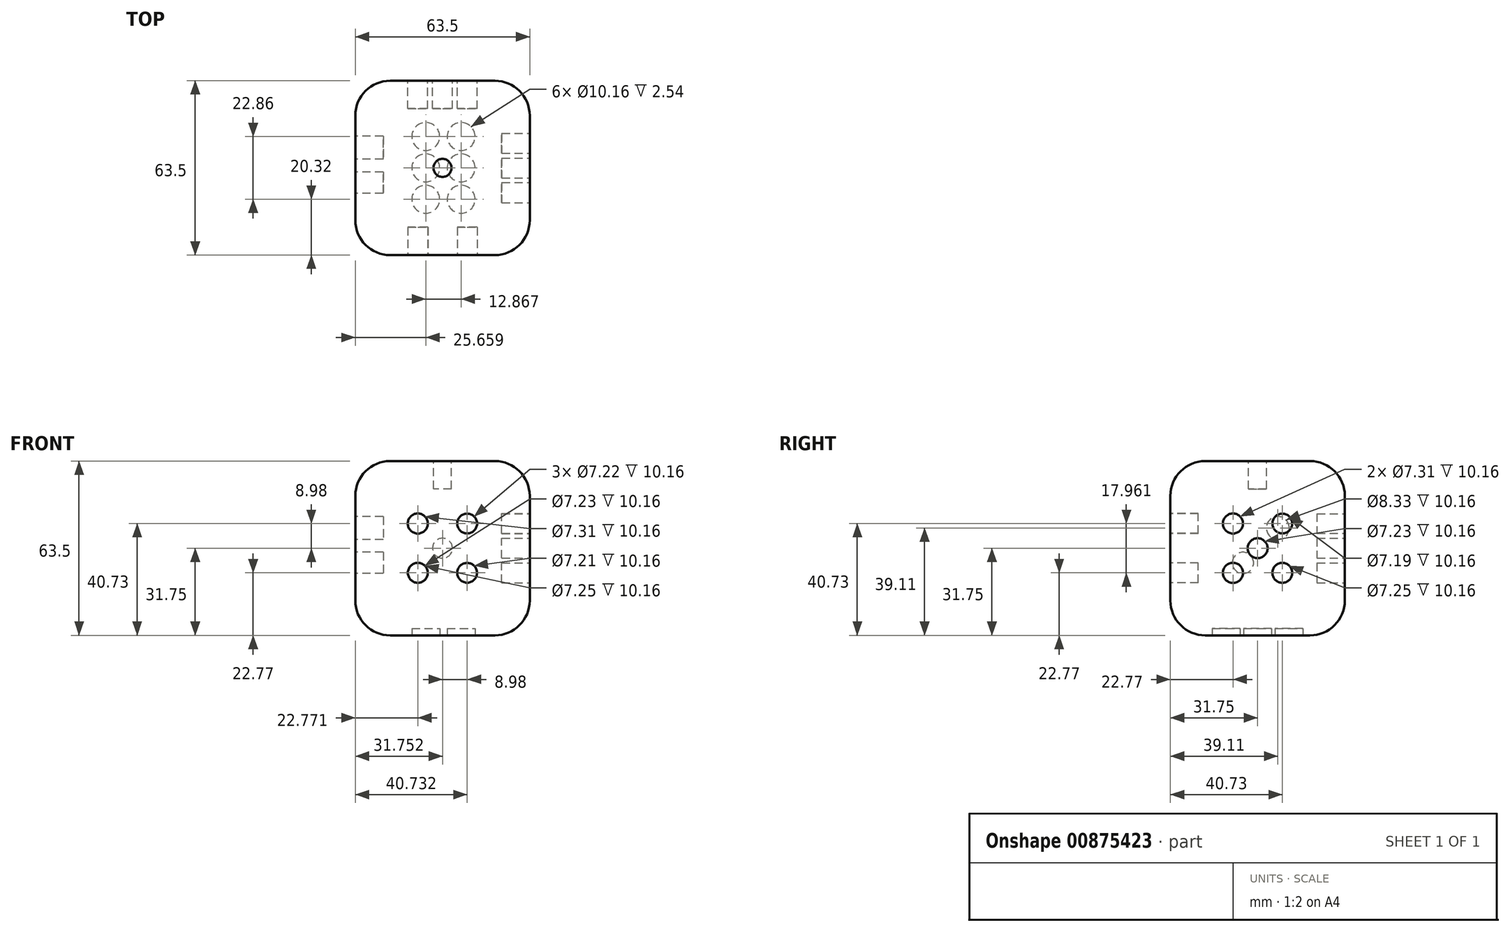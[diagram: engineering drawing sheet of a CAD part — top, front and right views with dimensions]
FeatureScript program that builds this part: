
annotation { "Feature Type Name" : "Feature", "Feature Type Description" : "" }
export const myFeature = defineFeature(function(context is Context, id is Id, definition is map)
    precondition{}
    {
        {
            var Q0;
            Q0=qCreatedBy(makeId("Top.planeOp"),FACE);
            var sketch = newSketch(context, id + "F0", { "sketchPlane" : qUnion([Q0])});
            skLineSegment(sketch, "E0.bottom", {"start": v(-137.5, 64.58) * mm, "end": v(-74, 64.58) * mm});
            skLineSegment(sketch, "E0.top", {"start": v(-137.5, 1.08) * mm, "end": v(-74, 1.08) * mm});
            skLineSegment(sketch, "E0.left", {"start": v(-137.5, 64.58) * mm, "end": v(-137.5, 1.08) * mm});
            skLineSegment(sketch, "E0.right", {"start": v(-74, 64.58) * mm, "end": v(-74, 1.08) * mm});
            skSolve(sketch);
        }
        {
            var Q0;
            Q0=makeQuery(id+"F0.imprint","IMPRINT",FACE,{"disambiguationData":[TD([[makeQuery(id+"F0.imprint","IMPRINT",EDGE,{"derivedFrom":sQuery(id+"F0.wireOp",EDGE,"E0.bottom")}),-1.0]])]});
            extrude(context, id + "F1", {"entities" : qUnion([Q0]), "depth" : 63.5 * mm, "offsetDistance" : 25.4 * mm});
        }
        {
            var Q0;
            Q0=makeQuery(id+"F1.opExtrude","CAP_EDGE",EDGE,{"disambiguationData":[OSD([sQuery(id+"F0.wireOp",EDGE,"E0.right")])],"isStart":true});
            var Q1;
            Q1=makeQuery(id+"F1.opExtrude","CAP_EDGE",EDGE,{"disambiguationData":[OSD([sQuery(id+"F0.wireOp",EDGE,"E0.left")])],"isStart":true});
            var Q2;
            Q2=makeQuery(id+"F1.opExtrude","CAP_EDGE",EDGE,{"disambiguationData":[OSD([sQuery(id+"F0.wireOp",EDGE,"E0.top")])],"isStart":true});
            var Q3;
            Q3=makeQuery(id+"F1.opExtrude","SWEPT_EDGE",EDGE,{"disambiguationData":[OSD([sQuery(id+"F0.wireOp",EDGE,"E0.top"),sQuery(id+"F0.wireOp",EDGE,"E0.left")])]});
            var Q4;
            Q4=makeQuery(id+"F1.opExtrude","SWEPT_EDGE",EDGE,{"disambiguationData":[OSD([sQuery(id+"F0.wireOp",EDGE,"E0.top"),sQuery(id+"F0.wireOp",EDGE,"E0.right")])]});
            var Q5;
            Q5=makeQuery(id+"F1.opExtrude","CAP_EDGE",EDGE,{"disambiguationData":[OSD([sQuery(id+"F0.wireOp",EDGE,"E0.left")])],"isStart":false});
            var Q6;
            Q6=makeQuery(id+"F1.opExtrude","CAP_EDGE",EDGE,{"disambiguationData":[OSD([sQuery(id+"F0.wireOp",EDGE,"E0.bottom")])],"isStart":true});
            var Q7;
            Q7=makeQuery(id+"F1.opExtrude","SWEPT_EDGE",EDGE,{"disambiguationData":[OSD([sQuery(id+"F0.wireOp",EDGE,"E0.bottom"),sQuery(id+"F0.wireOp",EDGE,"E0.left")])]});
            var Q8;
            Q8=makeQuery(id+"F1.opExtrude","CAP_EDGE",EDGE,{"disambiguationData":[OSD([sQuery(id+"F0.wireOp",EDGE,"E0.bottom")])],"isStart":false});
            var Q9;
            Q9=makeQuery(id+"F1.opExtrude","SWEPT_EDGE",EDGE,{"disambiguationData":[OSD([sQuery(id+"F0.wireOp",EDGE,"E0.bottom"),sQuery(id+"F0.wireOp",EDGE,"E0.right")])]});
            var Q10;
            Q10=makeQuery(id+"F1.opExtrude","CAP_EDGE",EDGE,{"disambiguationData":[OSD([sQuery(id+"F0.wireOp",EDGE,"E0.right")])],"isStart":false});
            var Q11;
            Q11=makeQuery(id+"F1.opExtrude","CAP_EDGE",EDGE,{"disambiguationData":[OSD([sQuery(id+"F0.wireOp",EDGE,"E0.top")])],"isStart":false});
            fillet(context, id + "F2", {"entities" : qUnion([Q0, Q1, Q2, Q3, Q4, Q5, Q6, Q7, Q8, Q9, Q10, Q11]), "radius" : 12.7 * mm, "tangentPropagation" : true, "allowEdgeOverflow" : false});
        }
        {
            var Q0;
            Q0=makeQuery(id+"F1.opExtrude","CAP_FACE",FACE,{"disambiguationData":[OSD([sQuery(id+"F0.wireOp",EDGE,"E0.bottom"),sQuery(id+"F0.wireOp",EDGE,"E0.top"),sQuery(id+"F0.wireOp",EDGE,"E0.left"),sQuery(id+"F0.wireOp",EDGE,"E0.right")])],"isStart":false});
            var sketch = newSketch(context, id + "F3", { "sketchPlane" : qUnion([Q0])});
            skLineSegment(sketch, "E1.0.0", {"start": v(-124.8, 13.78) * mm, "end": v(-86.7, 13.78) * mm});
            skLineSegment(sketch, "E1.0.1", {"start": v(-86.7, 13.78) * mm, "end": v(-86.7, 51.88) * mm});
            skLineSegment(sketch, "E1.0.2", {"start": v(-86.7, 51.88) * mm, "end": v(-124.8, 51.88) * mm});
            skLineSegment(sketch, "E1.0.3", {"start": v(-124.8, 51.88) * mm, "end": v(-124.8, 13.78) * mm});
            skLineSegment(sketch, "E2", {"start": v(-105.76, 51.88) * mm, "end": v(-105.76, 13.78) * mm, "construction": true});
            skLineSegment(sketch, "E3", {"start": v(-124.8, 32.83) * mm, "end": v(-86.7, 32.83) * mm, "construction": true});
            skCircle(sketch, "E4", {"center": v(-105.76, 32.83) * mm, "radius": 3.29 * mm});
            skSolve(sketch);
        }
        {
            var Q0;
            Q0=makeQuery(id+"F3.imprint","IMPRINT",FACE,{"disambiguationData":[TD([[makeQuery(id+"F3.imprint","IMPRINT",EDGE,{"derivedFrom":sQuery(id+"F3.wireOp",EDGE,"E4")}),1.0]])]});
            var Q1;
            Q1=sQuery(id+"F3.wireOp",EDGE,"E4");
            extrude(context, id + "F4", {"entities" : qUnion([Q0]), "operationType" : NewBodyOperationType.REMOVE, "surfaceEntities" : qUnion([Q1]), "oppositeDirection" : true, "depth" : 10.16 * mm, "offsetDistance" : 25.4 * mm});
        }
        {
            var Q0;
            Q0=makeQuery(id+"F1.opExtrude","CAP_FACE",FACE,{"disambiguationData":[OSD([sQuery(id+"F0.wireOp",EDGE,"E0.bottom"),sQuery(id+"F0.wireOp",EDGE,"E0.top"),sQuery(id+"F0.wireOp",EDGE,"E0.left"),sQuery(id+"F0.wireOp",EDGE,"E0.right")])],"isStart":true});
            var sketch = newSketch(context, id + "F5", { "sketchPlane" : qUnion([Q0])});
            skLineSegment(sketch, "E5.0.0", {"start": v(-124.8, -51.88) * mm, "end": v(-86.7, -51.88) * mm});
            skLineSegment(sketch, "E5.0.1", {"start": v(-86.7, -51.88) * mm, "end": v(-86.7, -13.78) * mm});
            skLineSegment(sketch, "E5.0.2", {"start": v(-86.7, -13.78) * mm, "end": v(-124.8, -13.78) * mm});
            skLineSegment(sketch, "E5.0.3", {"start": v(-124.8, -13.78) * mm, "end": v(-124.8, -51.88) * mm});
            skCircle(sketch, "E6", {"center": v(-111.85, -32.83) * mm, "radius": 5.08 * mm});
            skCircle(sketch, "E7", {"center": v(-111.85, -44.26) * mm, "radius": 5.08 * mm});
            skCircle(sketch, "E8", {"center": v(-98.98, -21.4) * mm, "radius": 5.08 * mm});
            skCircle(sketch, "E9", {"center": v(-98.98, -32.83) * mm, "radius": 5.08 * mm});
            skCircle(sketch, "E10", {"center": v(-98.98, -44.26) * mm, "radius": 5.08 * mm});
            skCircle(sketch, "E11", {"center": v(-111.85, -21.4) * mm, "radius": 5.08 * mm});
            skSolve(sketch);
        }
        {
            var Q0;
            Q0=makeQuery(id+"F5.imprint","IMPRINT",FACE,{"disambiguationData":[TD([[makeQuery(id+"F5.imprint","IMPRINT",EDGE,{"derivedFrom":sQuery(id+"F5.wireOp",EDGE,"E11")}),1.0]])]});
            var Q1;
            Q1=makeQuery(id+"F5.imprint","IMPRINT",FACE,{"disambiguationData":[TD([[makeQuery(id+"F5.imprint","IMPRINT",EDGE,{"derivedFrom":sQuery(id+"F5.wireOp",EDGE,"E8")}),1.0]])]});
            var Q2;
            Q2=makeQuery(id+"F5.imprint","IMPRINT",FACE,{"disambiguationData":[TD([[makeQuery(id+"F5.imprint","IMPRINT",EDGE,{"derivedFrom":sQuery(id+"F5.wireOp",EDGE,"E6")}),1.0]])]});
            var Q3;
            Q3=makeQuery(id+"F5.imprint","IMPRINT",FACE,{"disambiguationData":[TD([[makeQuery(id+"F5.imprint","IMPRINT",EDGE,{"derivedFrom":sQuery(id+"F5.wireOp",EDGE,"E9")}),1.0]])]});
            var Q4;
            Q4=makeQuery(id+"F5.imprint","IMPRINT",FACE,{"disambiguationData":[TD([[makeQuery(id+"F5.imprint","IMPRINT",EDGE,{"derivedFrom":sQuery(id+"F5.wireOp",EDGE,"E7")}),1.0]])]});
            var Q5;
            Q5=makeQuery(id+"F5.imprint","IMPRINT",FACE,{"disambiguationData":[TD([[makeQuery(id+"F5.imprint","IMPRINT",EDGE,{"derivedFrom":sQuery(id+"F5.wireOp",EDGE,"E10")}),1.0]])]});
            extrude(context, id + "F6", {"entities" : qUnion([Q0, Q1, Q2, Q3, Q4, Q5]), "operationType" : NewBodyOperationType.REMOVE, "oppositeDirection" : true, "depth" : 2.54 * mm, "offsetDistance" : 25.4 * mm});
        }
        {
            var Q0;
            Q0=makeQuery(id+"F1.opExtrude","SWEPT_FACE",FACE,{"disambiguationData":[OSD([sQuery(id+"F0.wireOp",EDGE,"E0.left")])]});
            var sketch = newSketch(context, id + "F7", { "sketchPlane" : qUnion([Q0])});
            skLineSegment(sketch, "E12.0.0", {"start": v(-51.88, 50.8) * mm, "end": v(-51.88, 12.7) * mm});
            skLineSegment(sketch, "E12.0.1", {"start": v(-51.88, 12.7) * mm, "end": v(-13.78, 12.7) * mm});
            skLineSegment(sketch, "E12.0.2", {"start": v(-13.78, 12.7) * mm, "end": v(-13.78, 50.8) * mm});
            skLineSegment(sketch, "E12.0.3", {"start": v(-13.78, 50.8) * mm, "end": v(-51.88, 50.8) * mm});
            skCircle(sketch, "E13", {"center": v(-40.19, 39.1) * mm, "radius": 4.16 * mm});
            skCircle(sketch, "E14", {"center": v(-27.49, 26.4) * mm, "radius": 3.88 * mm});
            skSolve(sketch);
        }
        {
            var Q0;
            Q0=makeQuery(id+"F7.imprint","IMPRINT",FACE,{"disambiguationData":[TD([[makeQuery(id+"F7.imprint","IMPRINT",EDGE,{"derivedFrom":sQuery(id+"F7.wireOp",EDGE,"E13")}),1.0]])]});
            var Q1;
            Q1=makeQuery(id+"F7.imprint","IMPRINT",FACE,{"disambiguationData":[TD([[makeQuery(id+"F7.imprint","IMPRINT",EDGE,{"derivedFrom":sQuery(id+"F7.wireOp",EDGE,"E14")}),1.0]])]});
            extrude(context, id + "F8", {"entities" : qUnion([Q0, Q1]), "operationType" : NewBodyOperationType.REMOVE, "oppositeDirection" : true, "depth" : 10.16 * mm, "offsetDistance" : 25.4 * mm});
        }
        {
            var Q0;
            Q0=makeQuery(id+"F1.opExtrude","SWEPT_FACE",FACE,{"disambiguationData":[OSD([sQuery(id+"F0.wireOp",EDGE,"E0.right")])]});
            var sketch = newSketch(context, id + "F9", { "sketchPlane" : qUnion([Q0])});
            skLineSegment(sketch, "E15.0.0", {"start": v(13.78, 50.8) * mm, "end": v(13.78, 12.7) * mm});
            skLineSegment(sketch, "E15.0.1", {"start": v(13.78, 12.7) * mm, "end": v(51.88, 12.7) * mm});
            skLineSegment(sketch, "E15.0.2", {"start": v(51.88, 12.7) * mm, "end": v(51.88, 50.8) * mm});
            skLineSegment(sketch, "E15.0.3", {"start": v(51.88, 50.8) * mm, "end": v(13.78, 50.8) * mm});
            skCircle(sketch, "E16", {"center": v(32.83, 31.75) * mm, "radius": 3.62 * mm});
            skCircle(sketch, "E17", {"center": v(23.85, 40.73) * mm, "radius": 3.65 * mm});
            skCircle(sketch, "E18", {"center": v(41.81, 22.77) * mm, "radius": 3.63 * mm});
            skCircle(sketch, "E19", {"center": v(41.81, 40.73) * mm, "radius": 3.6 * mm});
            skCircle(sketch, "E20", {"center": v(23.85, 22.77) * mm, "radius": 3.66 * mm});
            skSolve(sketch);
        }
        {
            var Q0;
            Q0=makeQuery(id+"F9.imprint","IMPRINT",FACE,{"disambiguationData":[TD([[makeQuery(id+"F9.imprint","IMPRINT",EDGE,{"derivedFrom":sQuery(id+"F9.wireOp",EDGE,"E17")}),1.0]])]});
            var Q1;
            Q1=makeQuery(id+"F9.imprint","IMPRINT",FACE,{"disambiguationData":[TD([[makeQuery(id+"F9.imprint","IMPRINT",EDGE,{"derivedFrom":sQuery(id+"F9.wireOp",EDGE,"E16")}),1.0]])]});
            var Q2;
            Q2=makeQuery(id+"F9.imprint","IMPRINT",FACE,{"disambiguationData":[TD([[makeQuery(id+"F9.imprint","IMPRINT",EDGE,{"derivedFrom":sQuery(id+"F9.wireOp",EDGE,"E19")}),1.0]])]});
            var Q3;
            Q3=makeQuery(id+"F9.imprint","IMPRINT",FACE,{"disambiguationData":[TD([[makeQuery(id+"F9.imprint","IMPRINT",EDGE,{"derivedFrom":sQuery(id+"F9.wireOp",EDGE,"E20")}),1.0]])]});
            var Q4;
            Q4=makeQuery(id+"F9.imprint","IMPRINT",FACE,{"disambiguationData":[TD([[makeQuery(id+"F9.imprint","IMPRINT",EDGE,{"derivedFrom":sQuery(id+"F9.wireOp",EDGE,"E18")}),1.0]])]});
            extrude(context, id + "F10", {"entities" : qUnion([Q0, Q1, Q2, Q3, Q4]), "operationType" : NewBodyOperationType.REMOVE, "oppositeDirection" : true, "depth" : 10.16 * mm, "offsetDistance" : 25.4 * mm});
        }
        {
            var Q0;
            Q0=makeQuery(id+"F1.opExtrude","SWEPT_FACE",FACE,{"disambiguationData":[OSD([sQuery(id+"F0.wireOp",EDGE,"E0.bottom")])]});
            var sketch = newSketch(context, id + "F11", { "sketchPlane" : qUnion([Q0])});
            skLineSegment(sketch, "E21.0.0", {"start": v(86.7, 50.8) * mm, "end": v(86.7, 12.7) * mm});
            skLineSegment(sketch, "E21.0.1", {"start": v(86.7, 12.7) * mm, "end": v(124.8, 12.7) * mm});
            skLineSegment(sketch, "E21.0.2", {"start": v(124.8, 12.7) * mm, "end": v(124.8, 50.8) * mm});
            skLineSegment(sketch, "E21.0.3", {"start": v(124.8, 50.8) * mm, "end": v(86.7, 50.8) * mm});
            skCircle(sketch, "E22", {"center": v(105.76, 31.75) * mm, "radius": 3.61 * mm});
            skCircle(sketch, "E23", {"center": v(96.78, 40.73) * mm, "radius": 3.6 * mm});
            skCircle(sketch, "E24", {"center": v(114.74, 22.77) * mm, "radius": 3.62 * mm});
            skSolve(sketch);
        }
        {
            var Q0;
            Q0=makeQuery(id+"F11.imprint","IMPRINT",FACE,{"disambiguationData":[TD([[makeQuery(id+"F11.imprint","IMPRINT",EDGE,{"derivedFrom":sQuery(id+"F11.wireOp",EDGE,"E23")}),1.0]])]});
            var Q1;
            Q1=makeQuery(id+"F11.imprint","IMPRINT",FACE,{"disambiguationData":[TD([[makeQuery(id+"F11.imprint","IMPRINT",EDGE,{"derivedFrom":sQuery(id+"F11.wireOp",EDGE,"E24")}),1.0]])]});
            var Q2;
            Q2=makeQuery(id+"F11.imprint","IMPRINT",FACE,{"disambiguationData":[TD([[makeQuery(id+"F11.imprint","IMPRINT",EDGE,{"derivedFrom":sQuery(id+"F11.wireOp",EDGE,"E22")}),1.0]])]});
            var Q3;
            Q3 = qSketchRegion(id + "F13", true);
            extrude(context, id + "F12", {"entities" : qUnion([Q0, Q1, Q2, Q3]), "operationType" : NewBodyOperationType.REMOVE, "oppositeDirection" : true, "depth" : 10.16 * mm, "offsetDistance" : 25.4 * mm});
        }
        {
            var Q0;
            Q0=makeQuery(id+"F1.opExtrude","SWEPT_FACE",FACE,{"disambiguationData":[OSD([sQuery(id+"F0.wireOp",EDGE,"E0.top")])]});
            var sketch = newSketch(context, id + "F13", { "sketchPlane" : qUnion([Q0])});
            skLineSegment(sketch, "E25.0.0", {"start": v(-124.8, 50.8) * mm, "end": v(-124.8, 12.7) * mm});
            skLineSegment(sketch, "E25.0.1", {"start": v(-124.8, 12.7) * mm, "end": v(-86.7, 12.7) * mm});
            skLineSegment(sketch, "E25.0.2", {"start": v(-86.7, 12.7) * mm, "end": v(-86.7, 50.8) * mm});
            skLineSegment(sketch, "E25.0.3", {"start": v(-86.7, 50.8) * mm, "end": v(-124.8, 50.8) * mm});
            skCircle(sketch, "E26", {"center": v(-96.78, 40.73) * mm, "radius": 3.6 * mm});
            skCircle(sketch, "E27", {"center": v(-114.74, 22.77) * mm, "radius": 3.62 * mm});
            skCircle(sketch, "E28", {"center": v(-114.74, 40.73) * mm, "radius": 3.65 * mm});
            skCircle(sketch, "E29", {"center": v(-96.78, 22.77) * mm, "radius": 3.6 * mm});
            skSolve(sketch);
        }
        {
            var Q0;
            Q0=makeQuery(id+"F13.imprint","IMPRINT",FACE,{"disambiguationData":[TD([[makeQuery(id+"F13.imprint","IMPRINT",EDGE,{"derivedFrom":sQuery(id+"F13.wireOp",EDGE,"E28")}),1.0]])]});
            var Q1;
            Q1=makeQuery(id+"F13.imprint","IMPRINT",FACE,{"disambiguationData":[TD([[makeQuery(id+"F13.imprint","IMPRINT",EDGE,{"derivedFrom":sQuery(id+"F13.wireOp",EDGE,"E26")}),1.0]])]});
            var Q2;
            Q2=makeQuery(id+"F13.imprint","IMPRINT",FACE,{"disambiguationData":[TD([[makeQuery(id+"F13.imprint","IMPRINT",EDGE,{"derivedFrom":sQuery(id+"F13.wireOp",EDGE,"E27")}),1.0]])]});
            var Q3;
            Q3=makeQuery(id+"F13.imprint","IMPRINT",FACE,{"disambiguationData":[TD([[makeQuery(id+"F13.imprint","IMPRINT",EDGE,{"derivedFrom":sQuery(id+"F13.wireOp",EDGE,"E29")}),1.0]])]});
            extrude(context, id + "F14", {"entities" : qUnion([Q0, Q1, Q2, Q3]), "operationType" : NewBodyOperationType.REMOVE, "oppositeDirection" : true, "depth" : 10.16 * mm, "offsetDistance" : 25.4 * mm});
        }
    });
